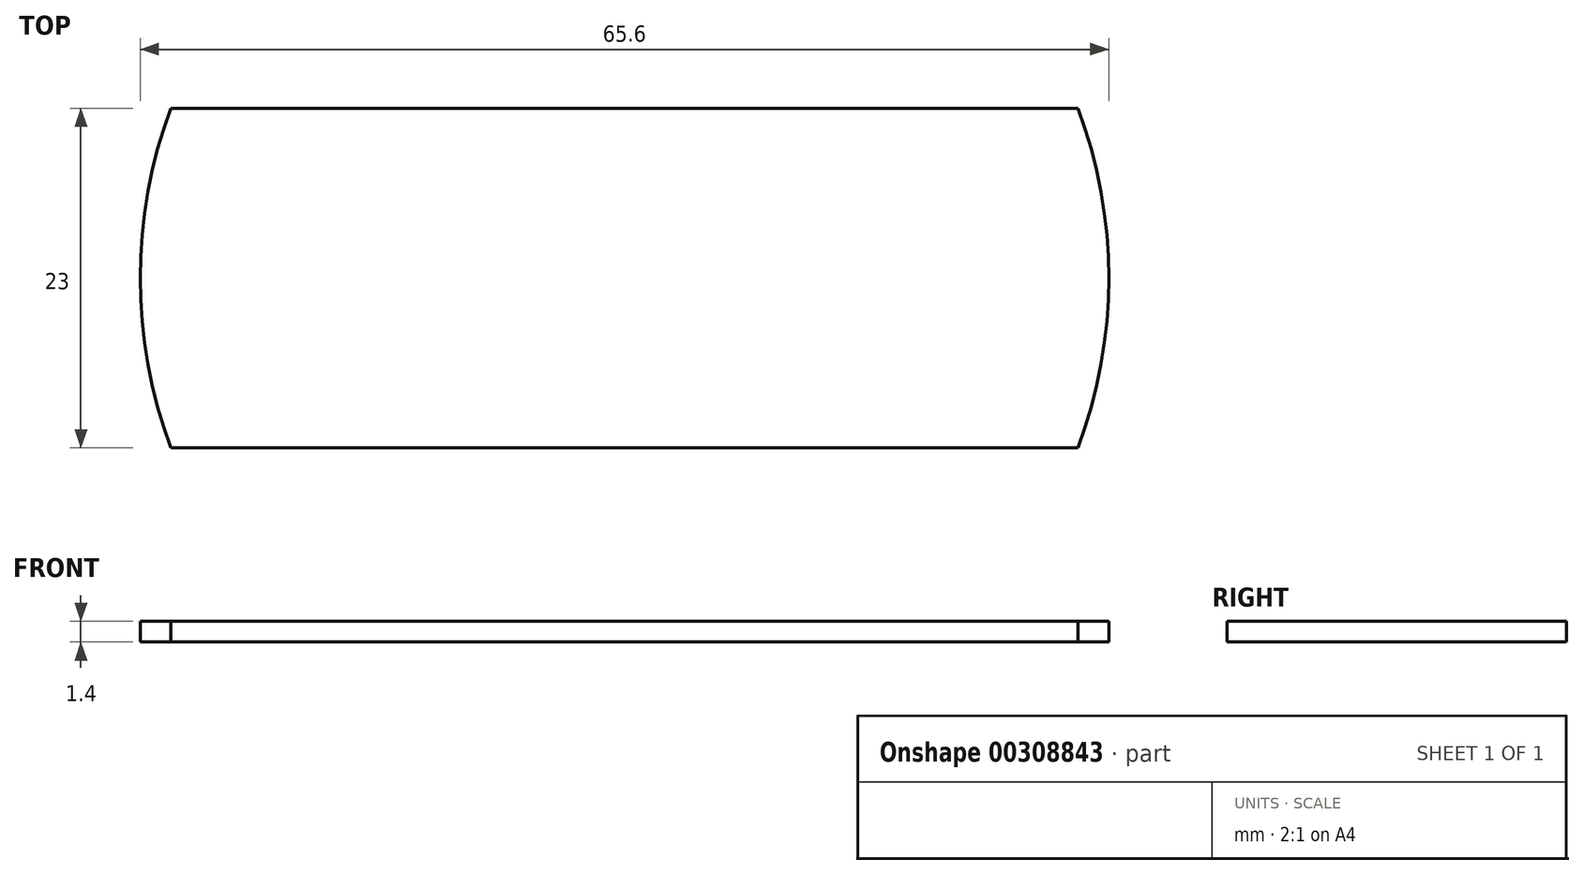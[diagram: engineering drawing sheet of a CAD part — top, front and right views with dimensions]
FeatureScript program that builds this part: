
annotation { "Feature Type Name" : "Feature", "Feature Type Description" : "" }
export const myFeature = defineFeature(function(context is Context, id is Id, definition is map)
    precondition{}
    {
        {
            var Q0;
            Q0=qCreatedBy(makeId("Top.planeOp"),FACE);
            var sketch = newSketch(context, id + "F0", { "sketchPlane" : qUnion([Q0])});
            skPoint(sketch, "E0.MirrorCS.start.orphan", {"position": v(-52.87, -12) * mm});
            skLineSegment(sketch, "E1", {"start": v(-26.5, -26.5) * mm, "end": v(0, -26.5) * mm, "construction": true});
            skLineSegment(sketch, "E2", {"start": v(0, -26.5) * mm, "end": v(0, -14.5) * mm, "construction": true});
            skLineSegment(sketch, "E3", {"start": v(0, -14.5) * mm, "end": v(30.2, -14.5) * mm, "construction": true});
            skLineSegment(sketch, "E4.MirrorCS", {"start": v(0, -26.5) * mm, "end": v(0, -38.5) * mm, "construction": true});
            skLineSegment(sketch, "E5.MirrorCS", {"start": v(0, -38.5) * mm, "end": v(30.2, -38.5) * mm, "construction": true});
            skLineSegment(sketch, "E6.MirrorCS", {"start": v(0, -14.5) * mm, "end": v(-30.2, -14.5) * mm, "construction": true});
            skLineSegment(sketch, "E7.MirrorCS", {"start": v(0, -38.5) * mm, "end": v(-30.2, -38.5) * mm, "construction": true});
            skArc(sketch, "E8", {"start": v(-30.2, -14.5) * mm, "mid": v(-32.5, -26.5) * mm, "end": v(-30.2, -38.5) * mm});
            skArc(sketch, "E9.trimOffspring", {"start": v(30.2, -38.5) * mm, "mid": v(32.5, -26.5) * mm, "end": v(30.2, -14.5) * mm});
            skLineSegment(sketch, "E10", {"start": v(0, -14.5) * mm, "end": v(0, -15) * mm, "construction": true});
            skLineSegment(sketch, "E11", {"start": v(0, -15) * mm, "end": v(30.4, -15) * mm});
            skLineSegment(sketch, "E12.MirrorCS", {"start": v(0, -15) * mm, "end": v(-30.4, -15) * mm});
            skLineSegment(sketch, "E13.MirrorCS", {"start": v(0, -38) * mm, "end": v(30.4, -38) * mm});
            skLineSegment(sketch, "E14.MirrorCS", {"start": v(0, -38) * mm, "end": v(-30.4, -38) * mm});
            skArc(sketch, "E15.0", {"start": v(30.48, -38.61) * mm, "mid": v(32.8, -26.5) * mm, "end": v(30.48, -14.39) * mm});
            skLineSegment(sketch, "E16", {"start": v(30.4, -15) * mm, "end": v(30.72, -15) * mm});
            skLineSegment(sketch, "E17", {"start": v(30.4, -38) * mm, "end": v(30.72, -38) * mm});
            skArc(sketch, "E18.0", {"start": v(-30.48, -14.39) * mm, "mid": v(-32.8, -26.5) * mm, "end": v(-30.48, -38.61) * mm});
            skLineSegment(sketch, "E19", {"start": v(-30.4, -38) * mm, "end": v(-30.72, -38) * mm});
            skLineSegment(sketch, "E20", {"start": v(-30.4, -15) * mm, "end": v(-30.72, -15) * mm});
            skSolve(sketch);
        }
        {
            var Q0;
            {var subQ1=sQuery(id+"F0.wireOp",EDGE,"W0cYEOpO-ICoy-FXKj-EsCo-HqiYgKbvXRLN");Q0=makeQuery(id+"F0.imprint","IMPRINT",FACE,{"disambiguationData":[TD([[makeQuery(id+"F0.imprint","IMPRINT",EDGE,{"derivedFrom":subQ1}),-1.0]])]});}
            var Q1;
            {var subQ0=sQuery(id+"F0.wireOp",EDGE,"U4bH4H1q-8tiJ-tKd0-QeQm-6Jlv5jcizuF3");Q1=makeQuery(id+"F0.imprint","IMPRINT",FACE,{"disambiguationData":[TD([[makeQuery(id+"F0.imprint","IMPRINT",EDGE,{"derivedFrom":subQ0}),-1.0]])]});}
            var Q2;
            {var subQ2=sQuery(id+"F0.wireOp",EDGE,"E11");Q2=makeQuery(id+"F0.imprint","IMPRINT",FACE,{"disambiguationData":[TD([[makeQuery(id+"F0.imprint","IMPRINT",EDGE,{"derivedFrom":subQ2}),-1.0]])]});}
            var Q3;
            {var subQ0=sQuery(id+"F0.wireOp",EDGE,"E16");Q3=makeQuery(id+"F0.imprint","IMPRINT",FACE,{"disambiguationData":[TD([[makeQuery(id+"F0.imprint","IMPRINT",EDGE,{"derivedFrom":subQ0}),-1.0]])]});}
            var Q4;
            {var subQ2=sQuery(id+"F0.wireOp",EDGE,"0df2e905-0fcb-4807-a5cc-46667c282828");Q4=makeQuery(id+"F0.imprint","IMPRINT",FACE,{"disambiguationData":[TD([[makeQuery(id+"F0.imprint","IMPRINT",EDGE,{"derivedFrom":subQ2}),-1.0]])]});}
            var Q5;
            {var subQ0=sQuery(id+"F0.wireOp",EDGE,"2bd7cf8c-4be2-4229-a89b-e4978b68d64c");Q5=makeQuery(id+"F0.imprint","IMPRINT",FACE,{"disambiguationData":[TD([[makeQuery(id+"F0.imprint","IMPRINT",EDGE,{"derivedFrom":subQ0}),-1.0]])]});}
            var Q6;
            {var subQ2=sQuery(id+"F0.wireOp",EDGE,"E19");Q6=makeQuery(id+"F0.imprint","IMPRINT",FACE,{"disambiguationData":[TD([[makeQuery(id+"F0.imprint","IMPRINT",EDGE,{"derivedFrom":subQ2}),-1.0]])]});}
            extrude(context, id + "F1", {"entities" : qUnion([Q0, Q1, Q2, Q3, Q4, Q5, Q6]), "oppositeDirection" : true, "depth" : 0.2 * mm});
        }
        {
            var Q0;
            {var subQ2=sQuery(id+"F0.wireOp",EDGE,"E19");Q0=makeQuery(id+"F0.imprint","IMPRINT",FACE,{"disambiguationData":[TD([[makeQuery(id+"F0.imprint","IMPRINT",EDGE,{"derivedFrom":subQ2}),-1.0]])]});}
            var Q1;
            {var subQ0=sQuery(id+"F0.wireOp",EDGE,"E16");Q1=makeQuery(id+"F0.imprint","IMPRINT",FACE,{"disambiguationData":[TD([[makeQuery(id+"F0.imprint","IMPRINT",EDGE,{"derivedFrom":subQ0}),-1.0]])]});}
            var Q2;
            {var subQ1=sQuery(id+"F0.wireOp",EDGE,"E11");Q2=makeQuery(id+"F0.imprint","IMPRINT",FACE,{"disambiguationData":[TD([[makeQuery(id+"F0.imprint","IMPRINT",EDGE,{"derivedFrom":subQ1}),-1.0]])]});}
            extrude(context, id + "F2", {"entities" : qUnion([Q0, Q1, Q2]), "operationType" : NewBodyOperationType.ADD, "depth" : 1.2 * mm});
        }
    });
